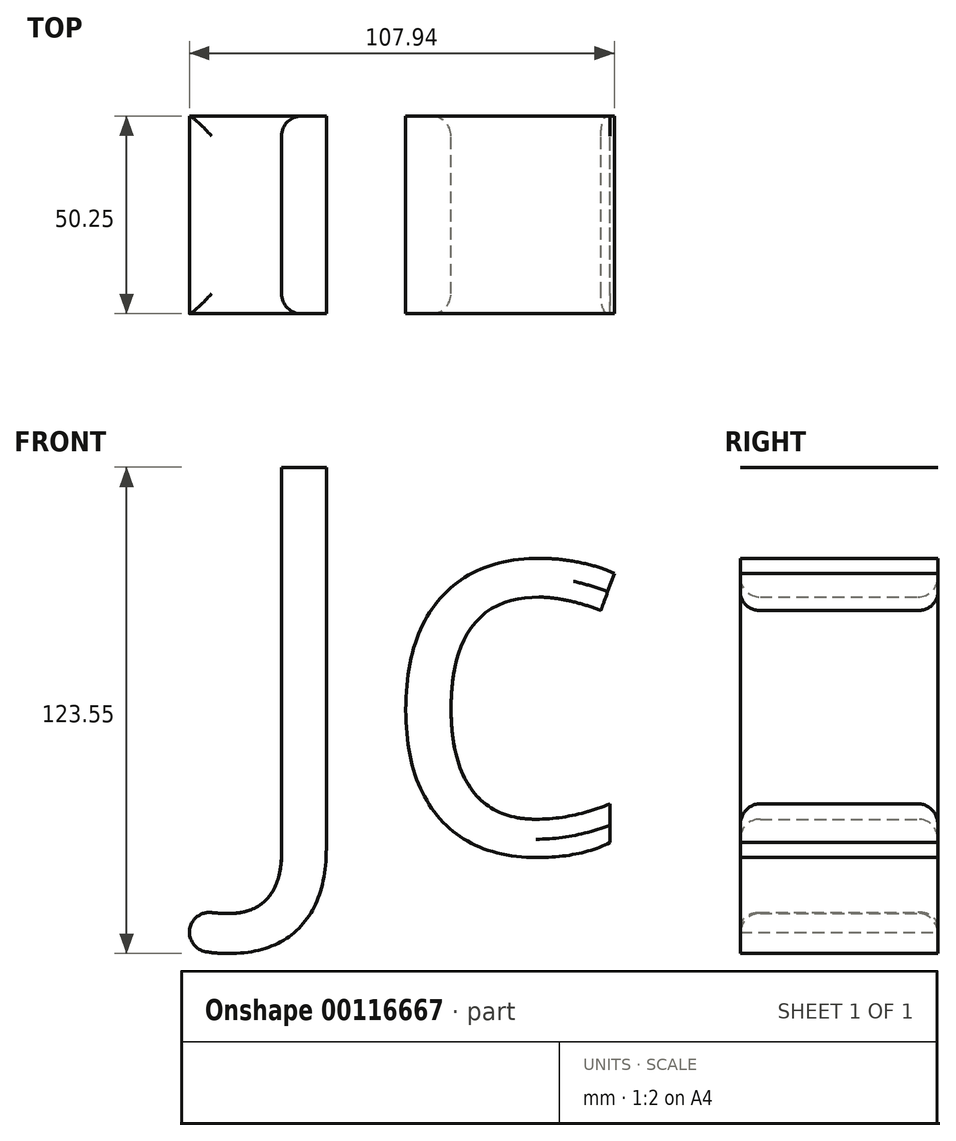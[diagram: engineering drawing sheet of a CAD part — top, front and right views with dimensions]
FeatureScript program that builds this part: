
annotation { "Feature Type Name" : "Feature", "Feature Type Description" : "" }
export const myFeature = defineFeature(function(context is Context, id is Id, definition is map)
    precondition{}
    {
        {
            var Q0;
            Q0=qCreatedBy(makeId("Front.planeOp"),FACE);
            var sketch = newSketch(context, id + "F0", { "sketchPlane" : qUnion([Q0])});
            skText(sketch, "E0", { "text": "Jc", "fontName": "OpenSans-Regular.ttf"});
            const initialGuessF0  = {"E0": [-0.05453, -0.04634, 1, 0, 0.09863]};
            skSetInitialGuess(sketch, initialGuessF0);
            skSolve(sketch);
        }
        {
            var Q0;
            Q0 = qSketchRegion(id + "F0", true);
            var Q1;
            Q1=makeQuery(id+"F0.imprint","IMPRINT",FACE,{"disambiguationData":[TD([[makeQuery(id+"F0.imprint","IMPRINT",EDGE,{"derivedFrom":sQuery(id+"F0.wireOp",EDGE,"E0.sketch_text.stroke-0")}),-1.0]])]});
            extrude(context, id + "F1", {"entities" : qUnion([Q0, Q1]), "depth" : 50.25 * mm});
        }
        {
            var Q0;
            Q0=makeQuery(id+"F1.opExtrude","CAP_EDGE",EDGE,{"disambiguationData":[OSD([sQuery(id+"F0.wireOp",EDGE,"E0.sketch_text.stroke-5")])],"isStart":false});
            var Q1;
            Q1=makeQuery(id+"F1.opExtrude","CAP_EDGE",EDGE,{"disambiguationData":[OSD([sQuery(id+"F0.wireOp",EDGE,"E0.sketch_text.stroke-5")])],"isStart":true});
            var Q2;
            Q2=makeQuery(id+"F1.opExtrude","SWEPT_EDGE",EDGE,{"disambiguationData":[OSD([sQuery(id+"F0.wireOp",EDGE,"E0.sketch_text.stroke-1"),sQuery(id+"F0.wireOp",EDGE,"E0.sketch_text.stroke-2")])]});
            var Q3;
            Q3=makeQuery(id+"F1.opExtrude","SWEPT_EDGE",EDGE,{"disambiguationData":[OSD([sQuery(id+"F0.wireOp",EDGE,"E0.sketch_text.stroke-0"),sQuery(id+"F0.wireOp",EDGE,"E0.sketch_text.stroke-1")])]});
            var Q4;
            Q4=makeQuery(id+"F1.opExtrude","CAP_EDGE",EDGE,{"disambiguationData":[OSD([sQuery(id+"F0.wireOp",EDGE,"E0.sketch_text.stroke-20")])],"isStart":true});
            var Q5;
            Q5=makeQuery(id+"F1.opExtrude","CAP_EDGE",EDGE,{"disambiguationData":[OSD([sQuery(id+"F0.wireOp",EDGE,"E0.sketch_text.stroke-19")])],"isStart":false});
            fillet(context, id + "F2", {"entities" : qUnion([Q0, Q1, Q2, Q3, Q4, Q5]), "radius" : 5.08 * mm, "tangentPropagation" : true, "allowEdgeOverflow" : false});
        }
    });
